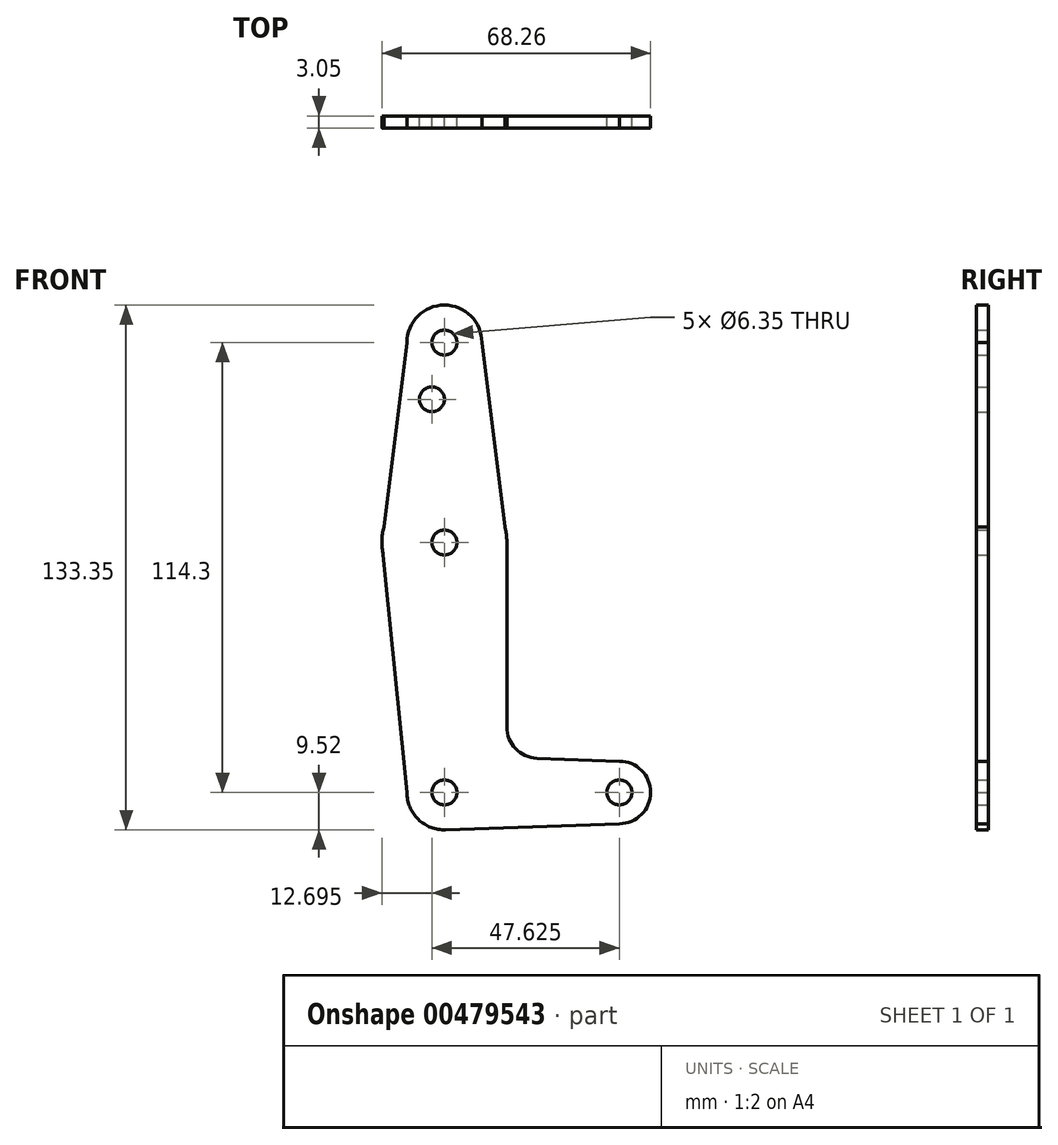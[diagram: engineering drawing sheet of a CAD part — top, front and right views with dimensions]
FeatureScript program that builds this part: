
annotation { "Feature Type Name" : "Feature", "Feature Type Description" : "" }
export const myFeature = defineFeature(function(context is Context, id is Id, definition is map)
    precondition{}
    {
        {
            var Q0;
            Q0=qCreatedBy(makeId("Front.planeOp"),FACE);
            var sketch = newSketch(context, id + "F0", { "sketchPlane" : qUnion([Q0])});
            skLineSegment(sketch, "E0", {"start": v(0, 114.3) * mm, "end": v(0, 0) * mm, "construction": true});
            skLineSegment(sketch, "E1", {"start": v(0, 0) * mm, "end": v(44.45, 0) * mm, "construction": true});
            skCircle(sketch, "E2", {"center": v(0, 114.3) * mm, "radius": 9.53 * mm});
            skCircle(sketch, "E3", {"center": v(0, 63.5) * mm, "radius": 15.88 * mm});
            skCircle(sketch, "E4", {"center": v(0, 0) * mm, "radius": 9.53 * mm});
            skCircle(sketch, "E5", {"center": v(44.45, 0) * mm, "radius": 7.94 * mm});
            skLineSegment(sketch, "E6", {"start": v(-9.53, 114.3) * mm, "end": v(-15.87, 63.5) * mm});
            skLineSegment(sketch, "E7", {"start": v(9.52, 114.3) * mm, "end": v(15.88, 63.5) * mm});
            skLineSegment(sketch, "E8", {"start": v(44.45, -7.94) * mm, "end": v(0.34, -9.52) * mm});
            skCircle(sketch, "E9", {"center": v(0, 114.3) * mm, "radius": 3.18 * mm});
            skCircle(sketch, "E10", {"center": v(-3.17, 99.89) * mm, "radius": 3.18 * mm});
            skCircle(sketch, "E11", {"center": v(0, 63.5) * mm, "radius": 3.18 * mm});
            skCircle(sketch, "E12", {"center": v(0, 0) * mm, "radius": 3.18 * mm});
            skCircle(sketch, "E13", {"center": v(44.45, 0) * mm, "radius": 3.18 * mm});
            skArc(sketch, "E14.filletArc", {"start": v(15.88, 16.63) * mm, "mid": v(18.1, 11.11) * mm, "end": v(23.54, 8.69) * mm});
            skLineSegment(sketch, "E15", {"start": v(15.88, 63.5) * mm, "end": v(15.88, 16.63) * mm});
            skLineSegment(sketch, "E16", {"start": v(23.54, 8.69) * mm, "end": v(44.45, 7.94) * mm});
            skLineSegment(sketch, "E17", {"start": v(-15.87, 63.5) * mm, "end": v(-9.53, 0) * mm});
            skSolve(sketch);
        }
        {
            var Q0;
            Q0 = qSketchRegion(id + "F0", true);
            extrude(context, id + "F1", {"entities" : qUnion([Q0]), "depth" : 3.05 * mm});
        }
    });
